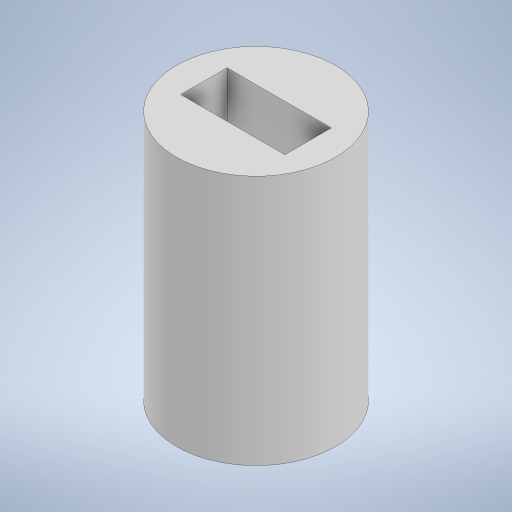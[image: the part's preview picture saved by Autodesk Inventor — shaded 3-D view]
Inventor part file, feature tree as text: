
AUTODESK INVENTOR PART (.ipt)
format: ipt  version: 2023 (Build 270158000, 158)  size: 360,960 bytes
history: native  units: in
note: dims shown in document units (in); Inventor stores cm internally (conversion verified against a paired STEP export)
features: extrude x3, sketch x3
ambient origin geometry x8: Origin, YZ Plane, XZ Plane, XY Plane, X Axis, Y Axis, Z Axis, Center Point
bodies: Solid1 (feature_tree)
feature tree (6):
  extrude  "Extrusion1"  Depth=0.5118in TaperAngle=0.0deg
  extrude  "Extrusion2"  Depth=0.315in TaperAngle=0.0deg
  extrude  "Extrusion3"  Depth=0.2126in
  sketch  "Sketch1"  dims[d0=0.3248in d1=0.5118in d2=0.0in]
  sketch  "Sketch2"  dims[d3=0.0787in d4=0.315in d5=0.0in]
  sketch  "Sketch3"  dims[d6=0.0945in d7=0.2126in d8=0.1969in d9=0.0in]
